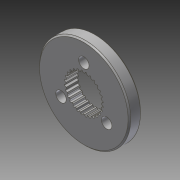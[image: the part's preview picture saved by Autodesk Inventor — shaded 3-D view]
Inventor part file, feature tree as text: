
AUTODESK INVENTOR PART (.ipt)
format: ipt  version: 2014 SP1 (Build 180222100, 222)  size: 322,048 bytes
history: native  units: in
note: dims shown in document units (in); Inventor stores cm internally (conversion verified against a paired STEP export)
features: chamfer x1, other x1, imported_body x1
ambient origin geometry x8: Origin, YZ Plane, XZ Plane, XY Plane, X Axis, Y Axis, Z Axis, Center Point
bodies: Body1 (feature_tree)
feature tree (3):
  chamfer  "Chamfer1"  [1 undecoded]
  other  "217-2625-008 Rev1.ipt1"
  imported_body  "Base1"
note: 1 required parameter value undecoded (feature->parameter linkage not recoverable at this tier; creation-order binding heuristic only, values carry confidence <= 0.55)
